# Revit family: xBasin-Undercounter-DXV-Pop_Round-D20055000_Series
name_source: partatom
category: Plumbing Fixtures
revit_build: Autodesk Revit 2014 (Build: 20130308_1515(x64)
units: mm (PartAtom-declared; Revit-internal decimal feet)

## types (3) — shared parameters
ADA Compliant = Yes
Assembly Code = D2010310
Basin Shape = Round
CW Connection = Yes
CWFU = 1.5
Cold Water Connection Diameter = 1/2"
Cold Water Connection Height = 22 3/4"
Cold Water Connection Radius = 1/4"
Cold Water Connection Width = 4"
Default Elevation = 34"
Description = Pop Round Under Counter Lavatory
HW Connection = Yes
HWFU = 1.5
Height = 7 1/2"
Hot Water Connection Diameter = 1/2"
Hot Water Connection Height = 22 3/4"
Hot Water Connection Radius = 1/4"
Hot Water Connection Width = 4"
Installation Type = Undercounter
Length = 14 5/8"
Manufacturer = DXV
Outlet Location = 3 1/16"
Price = Prices may vary. Please consult Manufacturer Representative for most up-to-date price list.
Product Documentation Link = https://dxv01.blob.core.windows.net
Product Page URL = https://www.dxv.com
URL = http://www.dxv.com
Vent Connection = No
WFU = 2
Warranty Documentation Link = https://www.dxv.com
Waste Connection = Yes
Waste Connection Diameter = 1 1/4"
Waste Connection Height = 20 1/4"
Waste Connection Radius = 5/8"
Width = 14 5/8"

## per-type parameters (varying)
| type | Finish | Material |
| D20055000.415 | Vitreous China-DXV-415-Canvas White | Vitreous China-DXV-415-Canvas White |
| D20055000.071 | Vitreous China-DXV-071-Biscuit | Vitreous China-DXV-071-Biscuit |
| D20055000.178 | Vitreous China-DXV-178-Black | Vitreous China-DXV-178-Black |

note: column(s) folded — value = type name in every type: Model

## geometry (parser evidence)
native form markers: Sweep x1
no freeform markers — native parametric forms only
